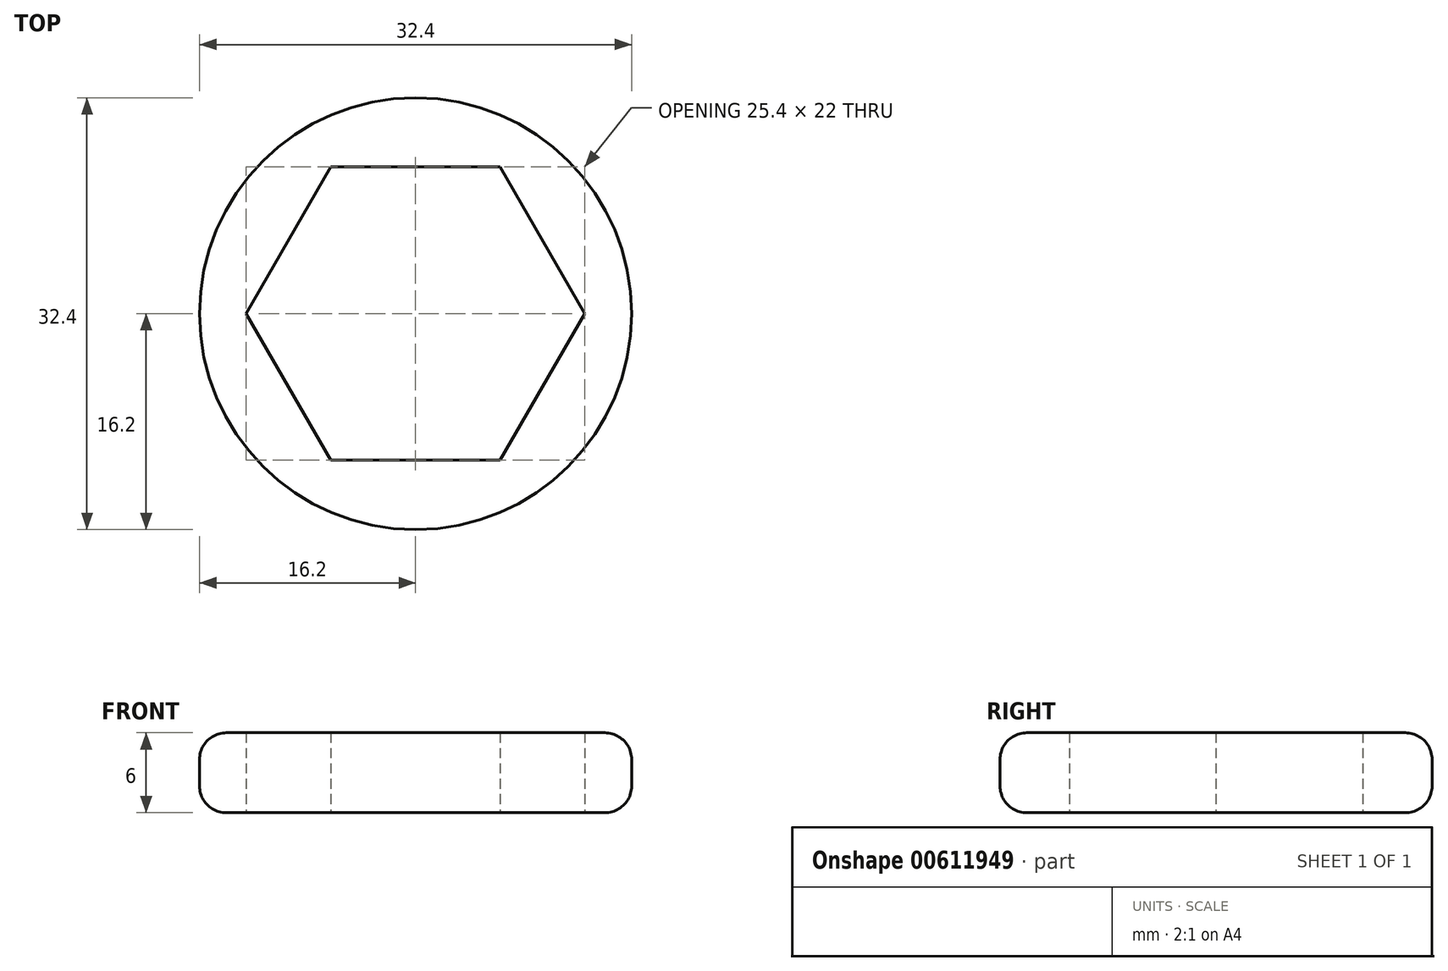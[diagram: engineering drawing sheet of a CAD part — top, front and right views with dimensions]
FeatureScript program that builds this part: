
annotation { "Feature Type Name" : "Feature", "Feature Type Description" : "" }
export const myFeature = defineFeature(function(context is Context, id is Id, definition is map)
    precondition{}
    {
        {
            var Q0;
            Q0=qCreatedBy(makeId("Top.planeOp"),FACE);
            var sketch = newSketch(context, id + "F0", { "sketchPlane" : qUnion([Q0])});
            skCircle(sketch, "E0.cCircle", {"center": v(0, 0) * mm, "radius": 11 * mm, "construction": true});
            skLineSegment(sketch, "E0.0", {"start": v(-6.35, 11) * mm, "end": v(6.35, 11) * mm});
            skLineSegment(sketch, "E0.1", {"start": v(6.35, 11) * mm, "end": v(12.7, 0) * mm});
            skLineSegment(sketch, "E0.2", {"start": v(12.7, 0) * mm, "end": v(6.35, -11) * mm});
            skLineSegment(sketch, "E0.3", {"start": v(6.35, -11) * mm, "end": v(-6.35, -11) * mm});
            skLineSegment(sketch, "E0.4", {"start": v(-6.35, -11) * mm, "end": v(-12.7, 0) * mm});
            skLineSegment(sketch, "E0.5", {"start": v(-12.7, 0) * mm, "end": v(-6.35, 11) * mm});
            skPoint(sketch, "E0.0.midPoint", {"position": v(0, 11) * mm});
            skCircle(sketch, "E1", {"center": v(0, 0) * mm, "radius": 16.2 * mm});
            skSolve(sketch);
        }
        {
            var Q0;
            Q0 = qSketchRegion(id + "F0", true);
            extrude(context, id + "F1", {"entities" : qUnion([Q0]), "depth" : 6 * mm, "offsetDistance" : 25 * mm});
        }
        {
            var Q0;
            Q0=makeQuery(id+"F1.opExtrude","CAP_EDGE",EDGE,{"disambiguationData":[OSD([sQuery(id+"F0.wireOp",EDGE,"E1")])],"isStart":false});
            var Q1;
            Q1=makeQuery(id+"F1.opExtrude","CAP_EDGE",EDGE,{"disambiguationData":[OSD([sQuery(id+"F0.wireOp",EDGE,"E1")])],"isStart":true});
            fillet(context, id + "F2", {"entities" : qUnion([Q0, Q1]), "radius" : 2 * mm, "tangentPropagation" : true, "allowEdgeOverflow" : false});
        }
    });
